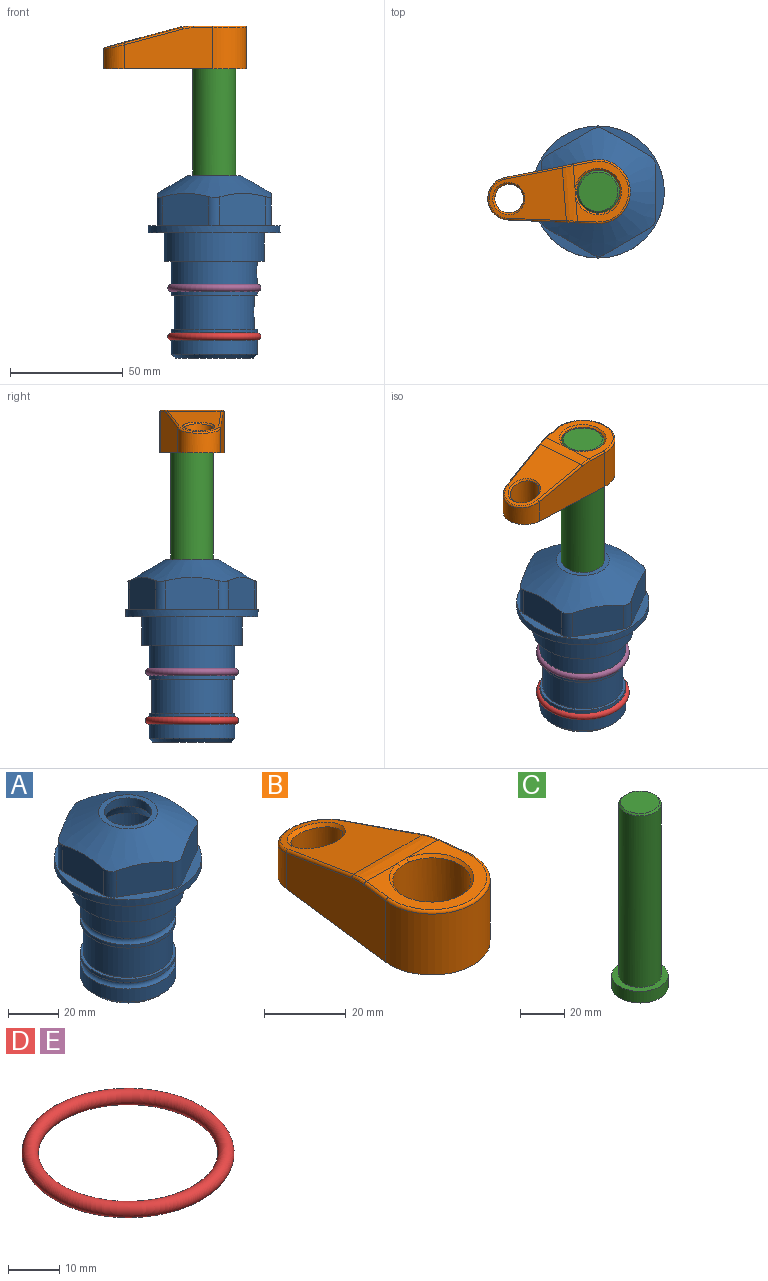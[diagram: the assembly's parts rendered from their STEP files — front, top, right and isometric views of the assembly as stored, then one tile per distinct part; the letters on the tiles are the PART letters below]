
ASSEMBLY  parts=5 mates=4
PART A: 36 faces, bbox 58.7x58.7x81 mm
  f0: cylinder r=17.78mm len=35.56mm, axis (0,0,1), area 1670.8mm2, adj f23,f24,f31
  f1: cylinder r=19.05mm len=38.1mm, axis (0,0,1), area 1191.9mm2, adj f26,f27,f30
  f2: plane 58.66x58.66mm, normal (0,0,-1), area 1150.6mm2, adj f3,f28
  f3: cylinder r=29.33mm len=58.66mm, axis (0,0,-1), area 585.1mm2, adj f2,f4
  f4: plane 58.66x58.66mm, normal (0,0,1), area 475.9mm2, adj f3,f5,f6,f7,f8,f9,f10,f11
  f5: plane 20.32x14.34mm, normal (-0.5,0.87,0), area 324.4mm2, adj f4,f15,f16,f17
  f6: plane 20.32x14.34mm, normal (0.5,0.87,0), area 324.4mm2, adj f4,f14,f15,f17
  f7: plane 23.48x14.34mm, normal (1,0,0), area 324.4mm2, adj f4,f13,f14,f17
  f8: plane 20.32x14.34mm, normal (0.5,-0.87,0), area 324.4mm2, adj f4,f12,f13,f17
  f9: plane 20.32x14.34mm, normal (-0.5,-0.87,0), area 324.4mm2, adj f4,f11,f12,f17
  f10: plane 23.48x14.34mm, normal (-1,0,0), area 324.4mm2, adj f4,f11,f16,f17
  f11: cylinder r=5.08mm len=12.85mm, axis (0,0,-1), area 67.2mm2, adj f4,f9,f10,f17
  f12: cylinder r=5.08mm len=12.85mm, axis (0,0,-1), area 67.2mm2, adj f4,f8,f9,f17
  f13: cylinder r=5.08mm len=12.85mm, axis (0,0,-1), area 67.2mm2, adj f4,f7,f8,f17
  f14: cylinder r=5.08mm len=12.85mm, axis (0,0,-1), area 67.2mm2, adj f4,f6,f7,f17
  f15: cylinder r=5.08mm len=12.85mm, axis (0,0,-1), area 67.2mm2, adj f4,f5,f6,f17
  f16: cylinder r=5.08mm len=12.85mm, axis (0,0,-1), area 67.2mm2, adj f4,f5,f10,f17
  f17: cone r=11.73mm half-angle=60deg, axis (0,0,-1), area 2071.8mm2, adj f5,f6,f7,f8,f9,f10,f11,f12
  f18: plane 23.46x23.46mm, normal (0,0,1), area 147.4mm2, adj f17,f35
  f19: plane 34.93x34.93mm, normal (0,0,-1), area 958mm2, adj f29
  f20: cylinder r=19.05mm len=38.1mm, axis (0,0,1), area 760.1mm2, adj f21,f29
  f21: torus R=19.05mm, axis (0,0,1), area 565.3mm2, adj f20,f22
  f22: cylinder r=19.05mm len=38.1mm, axis (0,0,1), area 190mm2, adj f21,f23
  f23: plane 38.1x38.1mm, normal (0,0,1), area 146.9mm2, adj f0,f22
  f24: plane 38.1x38.1mm, normal (0,0,-1), area 146.9mm2, adj f0,f25
  f25: cylinder r=19.05mm len=38.1mm, axis (0,0,1), area 190mm2, adj f24,f26
  f26: torus R=19.05mm, axis (0,0,1), area 565.3mm2, adj f1,f25
  f27: plane 44.45x44.45mm, normal (0,0,-1), area 411.7mm2, adj f1,f28
  f28: cylinder r=22.23mm len=44.45mm, axis (0,0,1), area 1773.5mm2, adj f2,f27
  f29: cone r=19.05mm half-angle=45deg, axis (0,0,1), area 257.5mm2, adj f19,f20
  f30: cylinder r=3.17mm len=6.75mm, axis (-1,0,0), area 128mm2, adj f1,f33
  f31: cylinder r=3.17mm len=6.35mm, axis (-1,0,0), area 102.5mm2, adj f0,f33
  f32: plane 25.4x25.4mm, normal (0,0,1), area 506.7mm2, adj f33
  f33: cylinder r=12.7mm len=66.42mm, axis (0,0,-1), area 5236.2mm2, adj f30,f31,f32,f34
  f34: cone r=9.53mm half-angle=30deg, axis (0,0,-1), area 443.4mm2, adj f33,f35
  f35: cylinder r=9.53mm len=19.05mm, axis (0,0,-1), area 240.9mm2, adj f18,f34
PART B: 31 faces, bbox 31.7x65.5x19.8 mm
  f0: plane 39.12x18.26mm, normal (0.99,0.12,0), area 612.2mm2, adj f1,f4,f7,f11,f13,f15
  f1: cylinder r=9.53mm len=18.91mm, axis (0,0,-1), area 296.1mm2, adj f0,f2,f7,f17
  f2: plane 39.12x18.26mm, normal (-0.99,0.12,0), area 612.2mm2, adj f1,f4,f7,f12,f14,f16
  f3: cylinder r=6.35mm len=12.7mm, axis (0,0,-1), area 362.4mm2, adj f7,f18
  f4: cylinder r=14.29mm len=28.58mm, axis (0,0,-1), area 882.2mm2, adj f0,f2,f7,f10
  f5: cylinder r=9.53mm len=19.05mm, axis (0,0,-1), area 1092.6mm2, adj f7,f19,f20
  f6: plane 26.99x23.69mm, normal (0,0,1), area 216.2mm2, adj f9,f10,f11,f12,f19
  f7: plane 63.5x28.58mm, normal (0,0,-1), area 661.8mm2, adj f0,f1,f2,f3,f4,f5,f22,f23
  f8: plane 33.52x23.6mm, normal (0,0.26,0.97), area 486mm2, adj f9,f15,f16,f17,f18
  f9: cylinder r=19.05mm len=24.72mm, axis (1,0,0), area 120.4mm2, adj f6,f8,f13,f14,f20
  f10: torus R=13.49mm, axis (0,0,1), area 59mm2, adj f4,f6,f11,f12
  f11: cylinder r=0.79mm len=8.67mm, axis (0.12,-0.99,0), area 10.8mm2, adj f0,f6,f10,f13
  f12: cylinder r=0.79mm len=8.67mm, axis (0.12,0.99,0), area 10.8mm2, adj f2,f6,f10,f14
  f13: bspline ~4.95x1.42mm, area 6.1mm2, adj f0,f9,f11,f15
  f14: bspline ~4.95x1.42mm, area 6.1mm2, adj f2,f9,f12,f16
  f15: cylinder r=0.79mm len=25.95mm, axis (0.12,-0.96,0.26), area 32.9mm2, adj f0,f8,f13,f17
  f16: cylinder r=0.79mm len=25.95mm, axis (0.12,0.96,-0.26), area 32.9mm2, adj f2,f8,f14,f17
  f17: bspline ~18.91x8.38mm, area 30mm2, adj f1,f8,f15,f16
  f18: bspline ~14.29x14.29mm, area 48.3mm2, adj f3,f8
  f19: cone r=9.53mm half-angle=45deg, axis (0,0,1), area 66.5mm2, adj f5,f6,f20
  f20: bspline ~3.22x0.96mm, area 3.5mm2, adj f5,f9,f19
  f21: plane 2.75x2.72mm, normal (0,0,-1), area 2.9mm2, adj f23,f25,f28
  f22: plane 23.05x15.88mm, normal (-0.99,-0.12,0), area 323.6mm2, adj f7,f25,f26,f27,f28,f29
  f23: plane 23.05x15.88mm, normal (0.99,-0.12,0), area 323.6mm2, adj f7,f21,f25,f27,f28,f30
  f24: cylinder r=9.53mm len=10.69mm, axis (0,0,-1), area 114.7mm2, adj f7,f27,f29,f30
  f25: cylinder r=12.7mm len=20.59mm, axis (0,0,-1), area 381.1mm2, adj f7,f21,f22,f23,f26,f28
  f26: plane 2.75x2.72mm, normal (0,0,-1), area 2.9mm2, adj f22,f25,f28
  f27: plane 19.72x18.37mm, normal (0,-0.26,-0.97), area 291.8mm2, adj f22,f23,f24,f28,f29,f30
  f28: cylinder r=15.88mm len=19.92mm, axis (1,0,0), area 54.8mm2, adj f21,f22,f23,f25,f26,f27
  f29: cylinder r=1.59mm len=11mm, axis (0,0,-1), area 34.7mm2, adj f7,f22,f24,f27
  f30: cylinder r=1.59mm len=11mm, axis (0,0,-1), area 34.7mm2, adj f7,f23,f24,f27
PART C: 6 faces, bbox 25.4x25.4x101.6 mm
  f0: plane 17.46x17.46mm, normal (0,0,1), area 239.5mm2, adj f5
  f1: plane 25.4x25.4mm, normal (0,0,-1), area 506.7mm2, adj f2
  f2: cylinder r=12.7mm len=25.4mm, axis (0,0,1), area 506.7mm2, adj f1,f3
  f3: plane 25.4x25.4mm, normal (0,0,1), area 221.7mm2, adj f2,f4
  f4: cylinder r=9.53mm len=94.46mm, axis (0,0,1), area 5653mm2, adj f3,f5
  f5: cone r=8.73mm half-angle=45deg, axis (0,0,-1), area 64.4mm2, adj f0,f4
PART D: 1 faces, bbox 44.7x44.7x3.2 mm
  f0: torus R=19.05mm, axis (0,0,1), area 1193.9mm2
PART E: same geometry as D
PLACE A at identity fixed
PLACE B rot(axis=(0,0,1),94.4deg) t=(0,0,28.35)mm
PLACE C rot(axis=(0,0,1),94.4deg) t=(0,0,27.55)mm
PLACE D t=(0,0,-21.59)mm
PLACE E at identity
MATE fastened D.f0 <-> A.f0  axis (0,0,1) through (0,0,-46.1)mm
MATE fastened E.f0 <-> A.f0  axis (0,0,1) through (0,0,-24.51)mm
MATE cylindrical A.f0 <-> C.f2  axis (0,0,1) through (0,0,-50.55)mm
MATE fastened B.f4 <-> C.f2  axis (0,0,-1) through (0,0,91.05)mm
